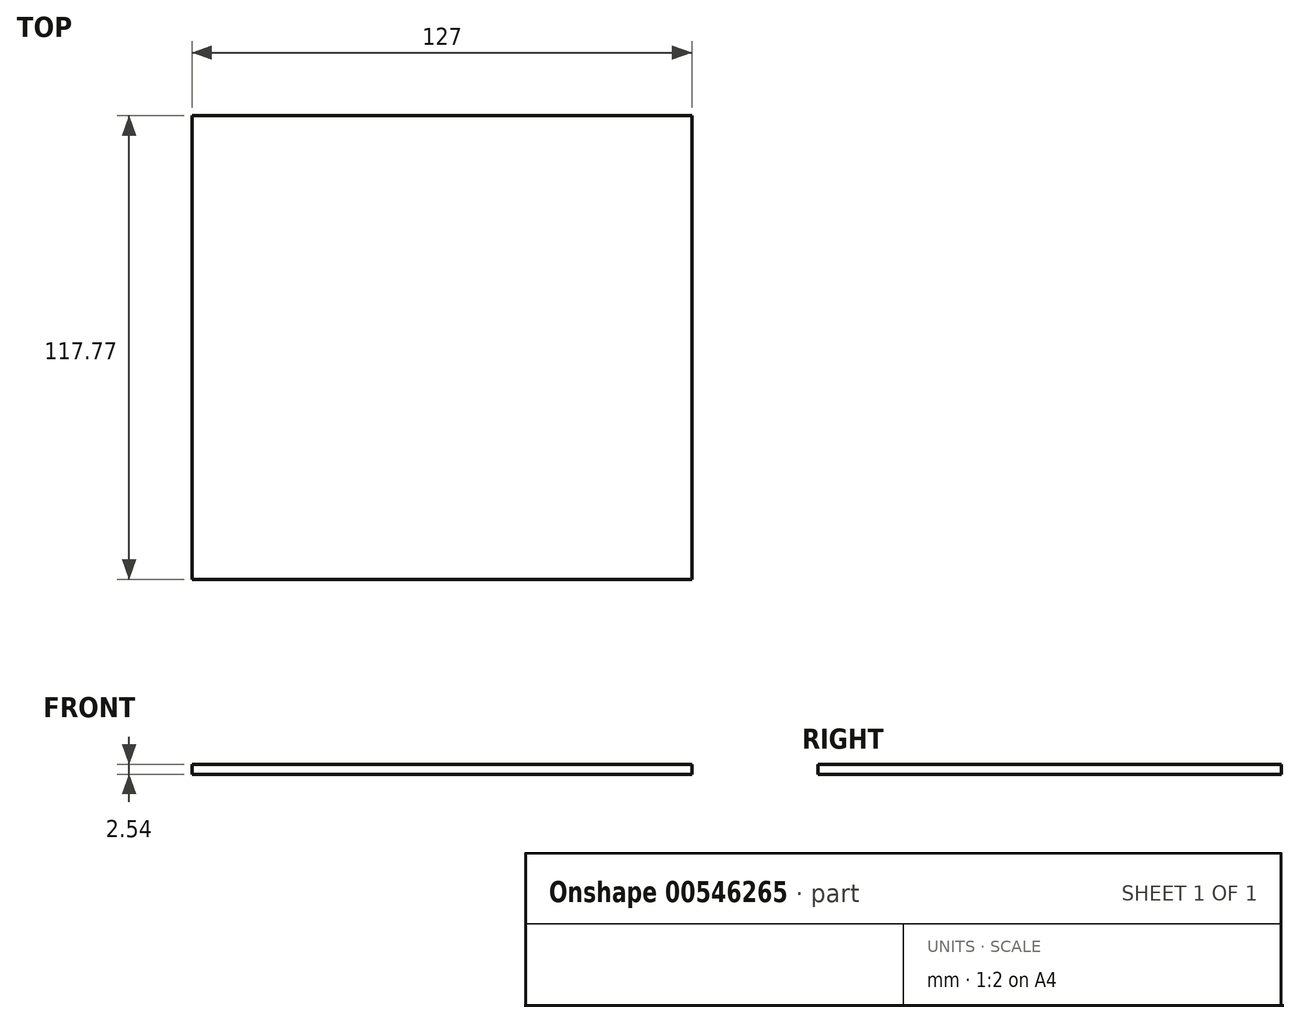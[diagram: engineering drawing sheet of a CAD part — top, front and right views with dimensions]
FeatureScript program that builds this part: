
annotation { "Feature Type Name" : "Feature", "Feature Type Description" : "" }
export const myFeature = defineFeature(function(context is Context, id is Id, definition is map)
    precondition{}
    {
        {
            var Q0;
            Q0=qCreatedBy(makeId("Top.planeOp"),FACE);
            var sketch = newSketch(context, id + "F0", { "sketchPlane" : qUnion([Q0])});
            skLineSegment(sketch, "E0.bottom", {"start": v(-60.02, 49.43) * mm, "end": v(66.98, 49.43) * mm});
            skLineSegment(sketch, "E0.top", {"start": v(-60.02, -68.34) * mm, "end": v(66.98, -68.34) * mm});
            skLineSegment(sketch, "E0.left", {"start": v(-60.02, 49.43) * mm, "end": v(-60.02, -68.34) * mm});
            skLineSegment(sketch, "E0.right", {"start": v(66.98, 49.43) * mm, "end": v(66.98, -68.34) * mm});
            skSolve(sketch);
        }
        {
            var Q0;
            Q0=makeQuery(id+"F0.imprint","IMPRINT",FACE,{"disambiguationData":[TD([[makeQuery(id+"F0.imprint","IMPRINT",EDGE,{"derivedFrom":sQuery(id+"F0.wireOp",EDGE,"E0.bottom")}),-1.0]])]});
            extrude(context, id + "F1", {"entities" : qUnion([Q0]), "depth" : 2.54 * mm, "offsetDistance" : 25.4 * mm});
        }
    });
